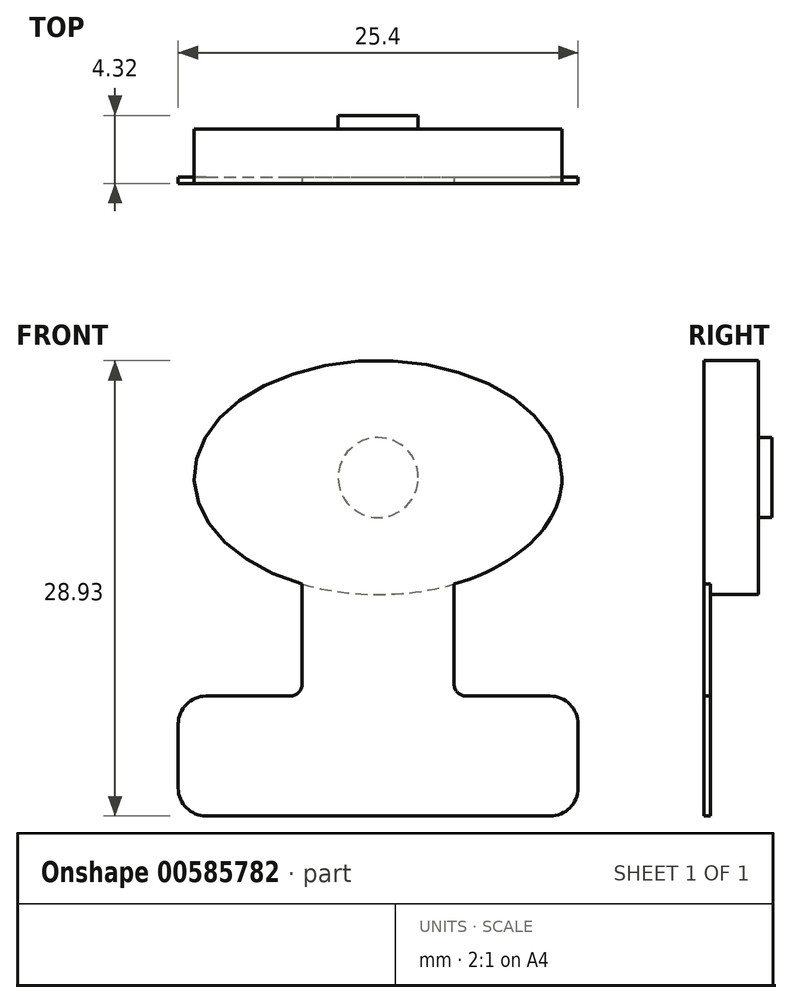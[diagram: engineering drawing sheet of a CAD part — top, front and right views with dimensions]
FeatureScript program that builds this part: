
annotation { "Feature Type Name" : "Feature", "Feature Type Description" : "" }
export const myFeature = defineFeature(function(context is Context, id is Id, definition is map)
    precondition{}
    {
        {
            var Q0;
            Q0=qCreatedBy(makeId("Front.planeOp"),FACE);
            var sketch = newSketch(context, id + "F0", { "sketchPlane" : qUnion([Q0])});
            skEllipse(sketch, "E0", {"center": v(0, 0) * mm, "majorRadius": 11.68 * mm, "minorRadius": 7.43 * mm, "majorAxis": v(1, 0)});
            skCircle(sketch, "E1", {"center": v(0, 0) * mm, "radius": 2.54 * mm});
            skLineSegment(sketch, "E2.bottom", {"start": v(-4.83, -6.77) * mm, "end": v(4.83, -6.77) * mm});
            skLineSegment(sketch, "E2.top", {"start": v(-4.83, -13.88) * mm, "end": v(4.83, -13.88) * mm});
            skLineSegment(sketch, "E2.left", {"start": v(-4.83, -6.77) * mm, "end": v(-4.83, -13.88) * mm});
            skLineSegment(sketch, "E2.right", {"start": v(4.83, -6.77) * mm, "end": v(4.83, -13.88) * mm});
            skLineSegment(sketch, "E3.bottom", {"start": v(-12.7, -13.88) * mm, "end": v(12.7, -13.88) * mm});
            skLineSegment(sketch, "E3.top", {"start": v(-12.7, -21.5) * mm, "end": v(12.7, -21.5) * mm});
            skLineSegment(sketch, "E3.left", {"start": v(-12.7, -13.88) * mm, "end": v(-12.7, -21.5) * mm});
            skLineSegment(sketch, "E3.right", {"start": v(12.7, -13.88) * mm, "end": v(12.7, -21.5) * mm});
            skLineSegment(sketch, "E4", {"start": v(0, 0) * mm, "end": v(0, -21.5) * mm, "construction": true});
            skPoint(sketch, "E5", {"position": v(0, -7.43) * mm});
            skFitSpline(sketch, "E6.0", {"points": [v(12.65, -0.89) * mm, v(12.72, 0) * mm, v(12.65, 0.89) * mm, v(12.38, 2.05) * mm, v(11.85, 3.15) * mm, v(11.1, 4.16) * mm, v(10.2, 5.11) * mm, v(8.86, 6.15) * mm, v(7.26, 6.99) * mm, v(5.84, 7.53) * mm, v(4.36, 7.97) * mm, v(2.81, 8.27) * mm, v(1.22, 8.42) * mm, v(0, 8.46) * mm, v(-1.22, 8.42) * mm, v(-2.81, 8.27) * mm, v(-4.36, 7.97) * mm, v(-5.84, 7.53) * mm, v(-7.26, 6.99) * mm, v(-8.86, 6.15) * mm, v(-10.2, 5.11) * mm, v(-11.1, 4.16) * mm, v(-11.85, 3.15) * mm, v(-12.38, 2.05) * mm, v(-12.65, 0.89) * mm, v(-12.72, 0) * mm, v(-12.65, -0.89) * mm, v(-12.38, -2.05) * mm, v(-11.85, -3.15) * mm, v(-11.1, -4.16) * mm, v(-10.2, -5.11) * mm, v(-8.86, -6.15) * mm, v(-7.26, -6.99) * mm, v(-5.84, -7.53) * mm, v(-4.36, -7.97) * mm, v(-2.81, -8.27) * mm, v(-1.22, -8.42) * mm, v(0, -8.46) * mm, v(1.22, -8.42) * mm, v(2.81, -8.27) * mm, v(4.36, -7.97) * mm, v(5.84, -7.53) * mm, v(7.26, -6.99) * mm, v(8.86, -6.15) * mm, v(10.2, -5.11) * mm, v(11.1, -4.16) * mm, v(11.85, -3.15) * mm, v(12.38, -2.05) * mm, v(12.65, -0.89) * mm, v(12.72, 0) * mm, v(12.65, 0.89) * mm, v(12.65, -0.89) * mm], "construction": true});
            skSolve(sketch);
        }
        {
            var Q0;
            Q0=makeQuery(id+"F0.imprint","IMPRINT",FACE,{"disambiguationData":[TD([[makeQuery(id+"F0.imprint","IMPRINT",EDGE,{"derivedFrom":sQuery(id+"F0.wireOp",EDGE,"E1")}),-1.0]])]});
            var Q1;
            Q1=makeQuery(id+"F0.imprint","IMPRINT",FACE,{"disambiguationData":[TD([[makeQuery(id+"F0.imprint","IMPRINT",EDGE,{"derivedFrom":sQuery(id+"F0.wireOp",EDGE,"E1")}),1.0]])]});
            var Q2;
            {var subQ0=sQuery(id+"F0.wireOp",EDGE,"E2.bottom");Q2=makeQuery(id+"F0.imprint","IMPRINT",FACE,{"disambiguationData":[TD([[makeQuery(id+"F0.imprint","IMPRINT",EDGE,{"derivedFrom":subQ0}),-1.0]])]});}
            extrude(context, id + "F1", {"entities" : qUnion([Q0, Q1, Q2]), "oppositeDirection" : true, "depth" : 3.45 * mm, "offsetDistance" : 25.4 * mm});
        }
        {
            var Q0;
            {var subQ0=sQuery(id+"F0.wireOp",EDGE,"E2.left");Q0=makeQuery(id+"F0.imprint","IMPRINT",FACE,{"disambiguationData":[TD([[makeQuery(id+"F0.imprint","IMPRINT",EDGE,{"derivedFrom":subQ0}),1.0]])]});}
            var Q1;
            Q1=makeQuery(id+"F0.imprint","IMPRINT",FACE,{"disambiguationData":[TD([[makeQuery(id+"F0.imprint","IMPRINT",EDGE,{"derivedFrom":sQuery(id+"F0.wireOp",EDGE,"E3.top")}),1.0]])]});
            extrude(context, id + "F2", {"entities" : qUnion([Q0, Q1]), "operationType" : NewBodyOperationType.ADD, "oppositeDirection" : true, "depth" : .4 * mm, "offsetDistance" : 25.4 * mm});
        }
        {
            var Q0;
            Q0=makeQuery(id+"F0.imprint","IMPRINT",FACE,{"disambiguationData":[TD([[makeQuery(id+"F0.imprint","IMPRINT",EDGE,{"derivedFrom":sQuery(id+"F0.wireOp",EDGE,"E1")}),1.0]])]});
            extrude(context, id + "F3", {"entities" : qUnion([Q0]), "operationType" : NewBodyOperationType.ADD, "oppositeDirection" : true, "depth" : 4.32 * mm, "offsetDistance" : 25.4 * mm});
        }
        {
            var Q0;
            Q0=makeQuery(id+"F2.opExtrude","SWEPT_EDGE",EDGE,{"disambiguationData":[OSD([sQuery(id+"F0.wireOp",EDGE,"E0"),sQuery(id+"F0.wireOp",EDGE,"E2.bottom"),sQuery(id+"F0.wireOp",EDGE,"E2.right")])]});
            var Q1;
            Q1=makeQuery(id+"F2.opExtrude","SWEPT_EDGE",EDGE,{"disambiguationData":[OSD([sQuery(id+"F0.wireOp",EDGE,"E0"),sQuery(id+"F0.wireOp",EDGE,"E2.bottom"),sQuery(id+"F0.wireOp",EDGE,"E2.left")])]});
            var Q2;
            Q2=makeQuery(id+"F2.opExtrude","SWEPT_EDGE",EDGE,{"disambiguationData":[OSD([sQuery(id+"F0.wireOp",EDGE,"E2.left"),sQuery(id+"F0.wireOp",EDGE,"E3.bottom")])]});
            var Q3;
            Q3=makeQuery(id+"F2.opExtrude","SWEPT_EDGE",EDGE,{"disambiguationData":[OSD([sQuery(id+"F0.wireOp",EDGE,"E2.right"),sQuery(id+"F0.wireOp",EDGE,"E3.bottom")])]});
            fillet(context, id + "F4", {"entities" : qUnion([Q0, Q1, Q2, Q3]), "radius" : 0.76 * mm, "tangentPropagation" : true, "allowEdgeOverflow" : false});
        }
        {
            var Q0;
            Q0=makeQuery(id+"F2.opExtrude","SWEPT_EDGE",EDGE,{"disambiguationData":[OSD([sQuery(id+"F0.wireOp",EDGE,"E3.bottom"),sQuery(id+"F0.wireOp",EDGE,"E3.right")])]});
            var Q1;
            Q1=makeQuery(id+"F2.opExtrude","SWEPT_EDGE",EDGE,{"disambiguationData":[OSD([sQuery(id+"F0.wireOp",EDGE,"E3.top"),sQuery(id+"F0.wireOp",EDGE,"E3.right")])]});
            var Q2;
            Q2=makeQuery(id+"F2.opExtrude","SWEPT_EDGE",EDGE,{"disambiguationData":[OSD([sQuery(id+"F0.wireOp",EDGE,"E3.bottom"),sQuery(id+"F0.wireOp",EDGE,"E3.left")])]});
            var Q3;
            Q3=makeQuery(id+"F2.opExtrude","SWEPT_EDGE",EDGE,{"disambiguationData":[OSD([sQuery(id+"F0.wireOp",EDGE,"E3.top"),sQuery(id+"F0.wireOp",EDGE,"E3.left")])]});
            fillet(context, id + "F5", {"entities" : qUnion([Q0, Q1, Q2, Q3]), "radius" : 1.78 * mm, "tangentPropagation" : true, "allowEdgeOverflow" : false});
        }
    });
